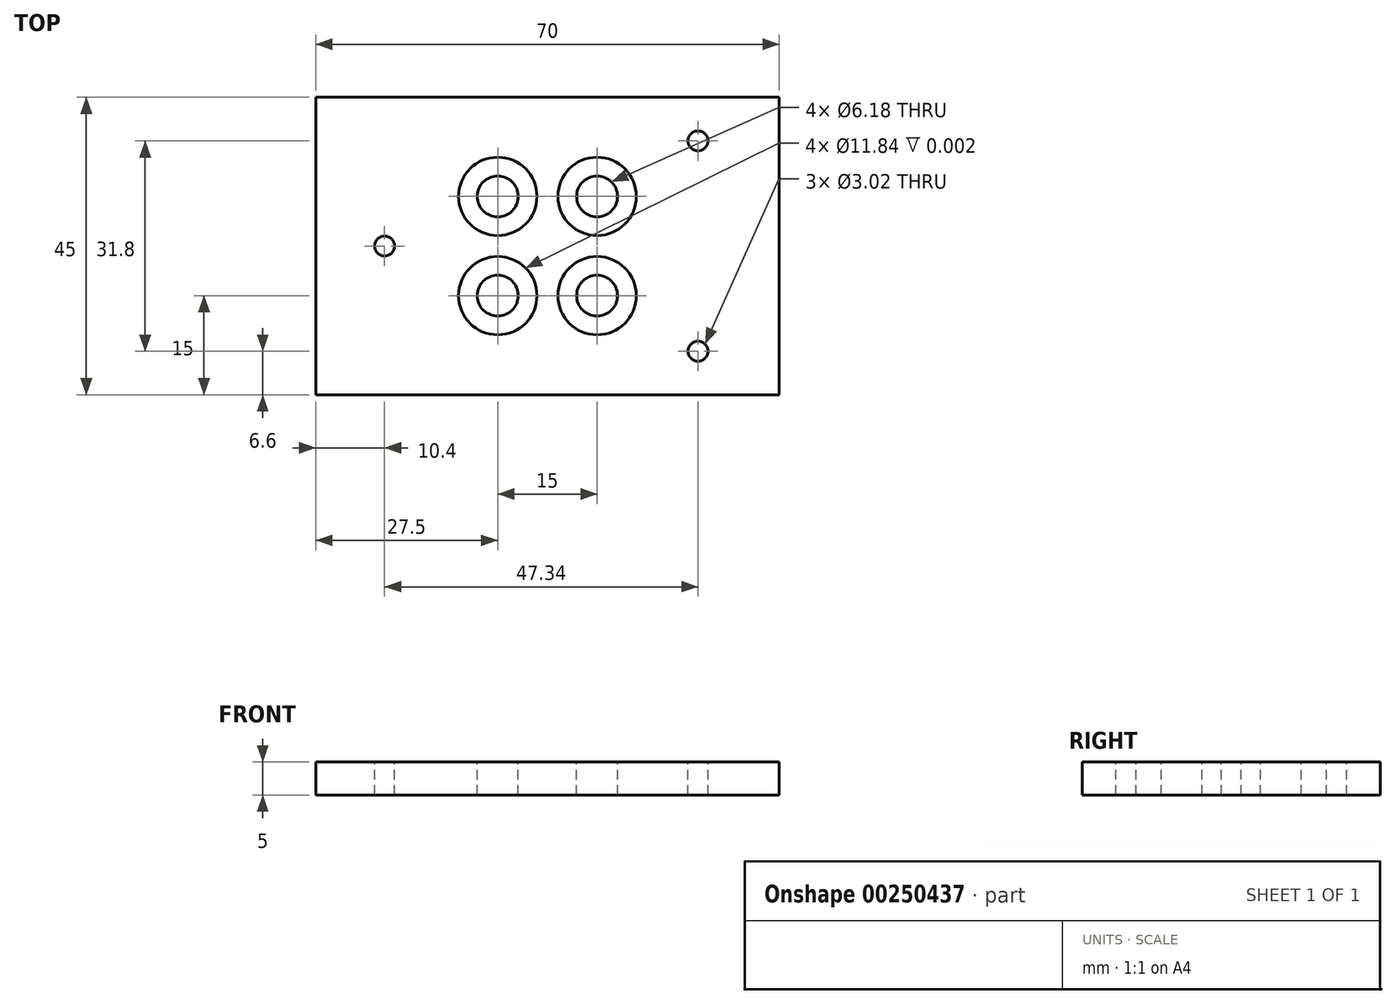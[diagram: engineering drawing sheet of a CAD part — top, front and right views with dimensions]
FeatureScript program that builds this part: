
annotation { "Feature Type Name" : "Feature", "Feature Type Description" : "" }
export const myFeature = defineFeature(function(context is Context, id is Id, definition is map)
    precondition{}
    {
        {
            var Q0;
            Q0=qCreatedBy(makeId("Top.planeOp"),FACE);
            var sketch = newSketch(context, id + "F0", { "sketchPlane" : qUnion([Q0])});
            skLineSegment(sketch, "E0", {"start": v(-34.2, -20) * mm, "end": v(-34.2, 11.8) * mm, "construction": true});
            skLineSegment(sketch, "E1", {"start": v(-34.2, 11.79) * mm, "end": v(-32.8, 11.79) * mm, "construction": true});
            skLineSegment(sketch, "E2", {"start": v(-32.8, 11.8) * mm, "end": v(-32.8, 20) * mm, "construction": true});
            skLineSegment(sketch, "E3", {"start": v(-32.8, 20) * mm, "end": v(21.8, 20) * mm, "construction": true});
            skLineSegment(sketch, "E4", {"start": v(21.8, 20) * mm, "end": v(32.8, 9.1) * mm, "construction": true});
            skLineSegment(sketch, "E5", {"start": v(32.8, 9.1) * mm, "end": v(32.8, -9.1) * mm, "construction": true});
            skLineSegment(sketch, "E6", {"start": v(32.8, -9.1) * mm, "end": v(21.8, -20) * mm, "construction": true});
            skLineSegment(sketch, "E7", {"start": v(-34.2, -20) * mm, "end": v(21.8, -20) * mm, "construction": true});
            skCircle(sketch, "E8", {"center": v(-25.3, 0) * mm, "radius": 1 * mm});
            skCircle(sketch, "E9", {"center": v(22.04, 15.9) * mm, "radius": 1 * mm});
            skCircle(sketch, "E10", {"center": v(22.04, -15.9) * mm, "radius": 1 * mm});
            skSolve(sketch);
        }
        {
            var Q0;
            Q0=qCreatedBy(makeId("Top.planeOp"),FACE);
            var sketch = newSketch(context, id + "F1", { "sketchPlane" : qUnion([Q0])});
            skLineSegment(sketch, "E11.bottom", {"start": v(-35.7, 22.5) * mm, "end": v(34.3, 22.5) * mm});
            skLineSegment(sketch, "E11.top", {"start": v(-35.7, -22.5) * mm, "end": v(34.3, -22.5) * mm});
            skLineSegment(sketch, "E11.left", {"start": v(-35.7, 22.5) * mm, "end": v(-35.7, -22.5) * mm});
            skLineSegment(sketch, "E11.right", {"start": v(34.3, 22.5) * mm, "end": v(34.3, -22.5) * mm});
            skSolve(sketch);
        }
        {
            var Q0;
            Q0=makeQuery(id+"F1.imprint","IMPRINT",FACE,{"disambiguationData":[TD([[makeQuery(id+"F1.imprint","IMPRINT",EDGE,{"derivedFrom":sQuery(id+"F1.wireOp",EDGE,"E11.bottom")}),-1.0]])]});
            extrude(context, id + "F2", {"entities" : qUnion([Q0]), "oppositeDirection" : true, "depth" : 5 * mm});
        }
        {
            var Q0;
            Q0=qCreatedBy(makeId("Top.planeOp"),FACE);
            var sketch = newSketch(context, id + "F3", { "sketchPlane" : qUnion([Q0])});
            skCircle(sketch, "E12.0", {"center": v(-25.3, 0) * mm, "radius": 1 * mm, "construction": true});
            skCircle(sketch, "E13.0", {"center": v(22.04, 15.9) * mm, "radius": 1 * mm, "construction": true});
            skCircle(sketch, "E14.0", {"center": v(22.04, -15.9) * mm, "radius": 1 * mm, "construction": true});
            skCircle(sketch, "E15", {"center": v(-25.3, 0) * mm, "radius": 1.5 * mm});
            skCircle(sketch, "E16", {"center": v(22.04, 15.9) * mm, "radius": 1.5 * mm});
            skCircle(sketch, "E17", {"center": v(22.04, -15.9) * mm, "radius": 1.5 * mm});
            skSolve(sketch);
        }
        {
            var Q0;
            Q0 = qSketchRegion(id + "F3", true);
            extrude(context, id + "F4", {"entities" : qUnion([Q0]), "operationType" : NewBodyOperationType.REMOVE, "oppositeDirection" : true, "depth" : 25 * mm});
        }
        {
            var Q0;
            Q0=qCreatedBy(makeId("Top.planeOp"),FACE);
            var sketch = newSketch(context, id + "F5", { "sketchPlane" : qUnion([Q0])});
            skLineSegment(sketch, "E18.bottom", {"start": v(-8.2, 7.5) * mm, "end": v(6.8, 7.5) * mm, "construction": true});
            skLineSegment(sketch, "E18.top", {"start": v(-8.2, -7.5) * mm, "end": v(6.8, -7.5) * mm, "construction": true});
            skLineSegment(sketch, "E18.left", {"start": v(-8.2, 7.5) * mm, "end": v(-8.2, -7.5) * mm, "construction": true});
            skLineSegment(sketch, "E18.right", {"start": v(6.8, 7.5) * mm, "end": v(6.8, -7.5) * mm, "construction": true});
            skLineSegment(sketch, "E19", {"start": v(-51.67, 0) * mm, "end": v(66.42, 0) * mm, "construction": true});
            skLineSegment(sketch, "E20", {"start": v(-0.7, 32.47) * mm, "end": v(-0.7, -44.14) * mm, "construction": true});
            skCircle(sketch, "E21", {"center": v(-8.2, 7.5) * mm, "radius": 3.09 * mm});
            skCircle(sketch, "E22", {"center": v(6.8, 7.5) * mm, "radius": 3.09 * mm});
            skCircle(sketch, "E23", {"center": v(-8.2, -7.5) * mm, "radius": 3.09 * mm});
            skCircle(sketch, "E24", {"center": v(6.8, -7.5) * mm, "radius": 3.09 * mm});
            skSolve(sketch);
        }
        {
            var Q0;
            Q0 = qSketchRegion(id + "F5", true);
            extrude(context, id + "F6", {"entities" : qUnion([Q0]), "operationType" : NewBodyOperationType.REMOVE, "oppositeDirection" : true, "depth" : 25 * mm});
        }
        {
            var Q0;
            Q0=makeQuery(id+"F2.opExtrude","CAP_FACE",FACE,{"disambiguationData":[OSD([sQuery(id+"F1.wireOp",EDGE,"E11.bottom"),sQuery(id+"F1.wireOp",EDGE,"E11.top"),sQuery(id+"F1.wireOp",EDGE,"E11.left"),sQuery(id+"F1.wireOp",EDGE,"E11.right")])],"isStart":true});
            var sketch = newSketch(context, id + "F7", { "sketchPlane" : qUnion([Q0])});
            skCircle(sketch, "E25", {"center": v(-8.2, 7.5) * mm, "radius": 5.92 * mm});
            skCircle(sketch, "E26", {"center": v(6.8, 7.5) * mm, "radius": 5.92 * mm});
            skCircle(sketch, "E27", {"center": v(-8.2, -7.5) * mm, "radius": 5.92 * mm});
            skCircle(sketch, "E28", {"center": v(6.8, -7.5) * mm, "radius": 5.92 * mm});
            skSolve(sketch);
        }
        {
            var Q0;
            Q0 = qSketchRegion(id + "F7", true);
            extrude(context, id + "F8", {"entities" : qUnion([Q0]), "operationType" : NewBodyOperationType.REMOVE, "oppositeDirection" : true, "depth" : 1 / 406.4 * mm});
        }
    });
